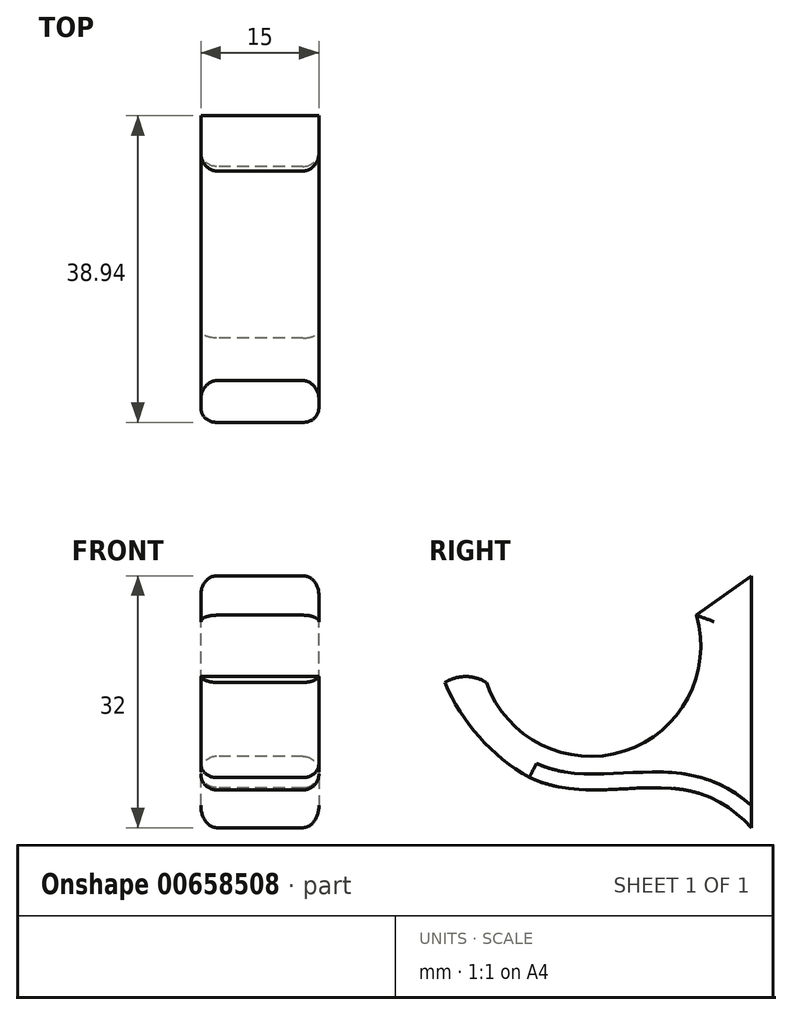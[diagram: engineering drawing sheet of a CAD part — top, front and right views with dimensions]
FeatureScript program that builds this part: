
annotation { "Feature Type Name" : "Feature", "Feature Type Description" : "" }
export const myFeature = defineFeature(function(context is Context, id is Id, definition is map)
    precondition{}
    {
        {
            var Q0;
            Q0=qCreatedBy(makeId("Right.planeOp"),FACE);
            var sketch = newSketch(context, id + "F0", { "sketchPlane" : qUnion([Q0])});
            skLineSegment(sketch, "E0", {"start": v(0, 0) * mm, "end": v(0, 32) * mm});
            skLineSegment(sketch, "E1", {"start": v(0, 32) * mm, "end": v(-7, 27) * mm});
            skArc(sketch, "E2", {"start": v(-33.65, 18.45) * mm, "mid": v(-16.16, 9.73) * mm, "end": v(-7, 27) * mm});
            skArc(sketch, "E3", {"start": v(-33.65, 18.45) * mm, "mid": v(-36.3, 19.2) * mm, "end": v(-38.94, 18.45) * mm});
            skArc(sketch, "E4", {"start": v(-38.94, 18.45) * mm, "mid": v(-34.57, 11.53) * mm, "end": v(-28.22, 6.36) * mm});
            skFitSpline(sketch, "E5", {"points": [v(-28.22, 6.36) * mm, v(0, 0) * mm], "startDerivative": vector(30.25, -13.4) * mm, "endDerivative": vector(26.07, -28.48) * mm});
            skSolve(sketch);
        }
        {
            var Q0;
            Q0=makeQuery(id+"F0.imprint","IMPRINT",FACE,{"disambiguationData":[TD([[makeQuery(id+"F0.imprint","IMPRINT",EDGE,{"derivedFrom":sQuery(id+"F0.wireOp",EDGE,"E0")}),1.0]])]});
            extrude(context, id + "F1", {"entities" : qUnion([Q0]), "depth" : 15 * mm, "offsetDistance" : 25 * mm});
        }
        {
            var Q0;
            Q0=makeQuery(id+"F1.opExtrude","CAP_EDGE",EDGE,{"disambiguationData":[OSD([sQuery(id+"F0.wireOp",EDGE,"E2")])],"isStart":false});
            var Q1;
            Q1=makeQuery(id+"F1.opExtrude","CAP_EDGE",EDGE,{"disambiguationData":[OSD([sQuery(id+"F0.wireOp",EDGE,"E2")])],"isStart":true});
            var Q2;
            Q2=makeQuery(id+"F1.opExtrude","CAP_EDGE",EDGE,{"disambiguationData":[OSD([sQuery(id+"F0.wireOp",EDGE,"E1")])],"isStart":true});
            var Q3;
            Q3=makeQuery(id+"F1.opExtrude","CAP_EDGE",EDGE,{"disambiguationData":[OSD([sQuery(id+"F0.wireOp",EDGE,"E1")])],"isStart":false});
            var Q4;
            Q4=makeQuery(id+"F1.opExtrude","CAP_EDGE",EDGE,{"disambiguationData":[OSD([sQuery(id+"F0.wireOp",EDGE,"E5")])],"isStart":false});
            var Q5;
            Q5=makeQuery(id+"F1.opExtrude","CAP_EDGE",EDGE,{"disambiguationData":[OSD([sQuery(id+"F0.wireOp",EDGE,"E4")])],"isStart":false});
            var Q6;
            Q6=makeQuery(id+"F1.opExtrude","CAP_EDGE",EDGE,{"disambiguationData":[OSD([sQuery(id+"F0.wireOp",EDGE,"E4")])],"isStart":true});
            var Q7;
            Q7=makeQuery(id+"F1.opExtrude","CAP_EDGE",EDGE,{"disambiguationData":[OSD([sQuery(id+"F0.wireOp",EDGE,"E5")])],"isStart":true});
            fillet(context, id + "F2", {"entities" : qUnion([Q0, Q1, Q2, Q3, Q4, Q5, Q6, Q7]), "radius" : 2 * mm, "tangentPropagation" : true, "allowEdgeOverflow" : false});
        }
    });
